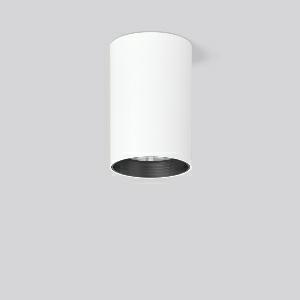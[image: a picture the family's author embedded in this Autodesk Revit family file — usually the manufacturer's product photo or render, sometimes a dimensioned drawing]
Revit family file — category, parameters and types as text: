
# Revit family: heledon_maxi_a_931227_002_1_a9ca
name_source: partatom
category: Lighting Fixtures
units: mm (PartAtom-declared; Revit-internal decimal feet)

## family parameters
Cut with Voids When Loaded = No
Host = Face
Light Source = No
Part Type = Normal
Room Calculation Point = No
Round Connector Dimension = Use Diameter
Shared = No

## types (1)
- HELEDON maxi A (1 x LED Modul 940, 3900 lm, 4000)
    Apparent Load = 35 VA
    Approval mark = CE
    CIE Flux Codes = 97 100 100 100 100
    Color Rendering = 92
    Color Temperature = 4000
    Default Elevation = 1800 mm
    Description = Series: HELEDON maxi
Cylindrical surface-mounted downlight. Housing: die-cast aluminium, powder-coated. Internal ceiling frame polycarbonate with bayonet mounting. Black plastic ring and recessed LED to prevent glare from the side. Optical assembly with lens made of plastic (polycarbonate) for the best homogeneous light distribution - can be changed without tools. Best colour rendering index Ra>90. Suitable for Ceiling mounting. Easy installation with a separate ceiling frame with bayonet mounting and plug connection. Driver integrated. Connected via plug-in connector. High quality converter without flickering and stroboscopic effect. The following accessories can be mounted without use of tools: interchangeable lenses, decorative glasses, honeycomb louvre, clear and frosted diffusers, white interchangeable plastic ring. 
Colour: traffic white, matt (RAL 9016)
Diameter: 123 mm
Height: 183 mm
Lamp: LED
Socket: without socket
Colour temperature: 4000K
Colour rendering index (CRI): 92
System power: 35 W
Rated luminous flux: 3900 lm
Luminous efficiency: 111 lm/W
Control gear: Regulated power supply
Protection class: I
Type of protection: IP 20
    Height = 183 mm
    Lamp = 1 x LED Modul 940
    Lamp Light Flux = 3900 lm
    Lamp count = 1
    Length = 123 mm
    Lifetime = 50000 h
    Luminous efficacy = 111 lm/W
    Manufacturer = RZB
    ModVariant = No
    Model = 931227.002.1
    Mounting Place = Ceiling
    Mounting Type = Surface mounted
    Number of Poles = 1
    OnlyDefault = Yes
    Power Factor = 1
    Product Name = HELEDON maxi A
    Product group = Surface mounted downlights
    ProductGroupID = 302
    Protection Class = Protection class I
    Protection Degree = IP 20
    RLX_Detail_Level = 1
    RLX_Emergency_Light_Flux = 0 lm
    RLX_Emergency_Type = 0
    RLX_Emergency_Type_DB = No
    RlxData = <blob elided: 97233 chars, md5=ccc17dae>
    Socket = socket
    Standby Power = 0 W
    System Light Flux = 3900 lm
    System Power = 35 W
    Type Comments = Product without accessories
    Type Image = 931193.002.jpg
    URL = http://relux.com
    VarID = ---
    Voltage = 230 V
    Voltage Range = 220-240 V
    Weight = 0.00 kg
    Width = 0 mm  [stored 0 ft]

note: [stored X ft] marks values corroborated as IEEE doubles in the binary element streams (Revit-internal decimal feet)

## geometry (parser evidence)
native form markers: Blend x4, Sweep x8
no freeform markers — native parametric forms only
